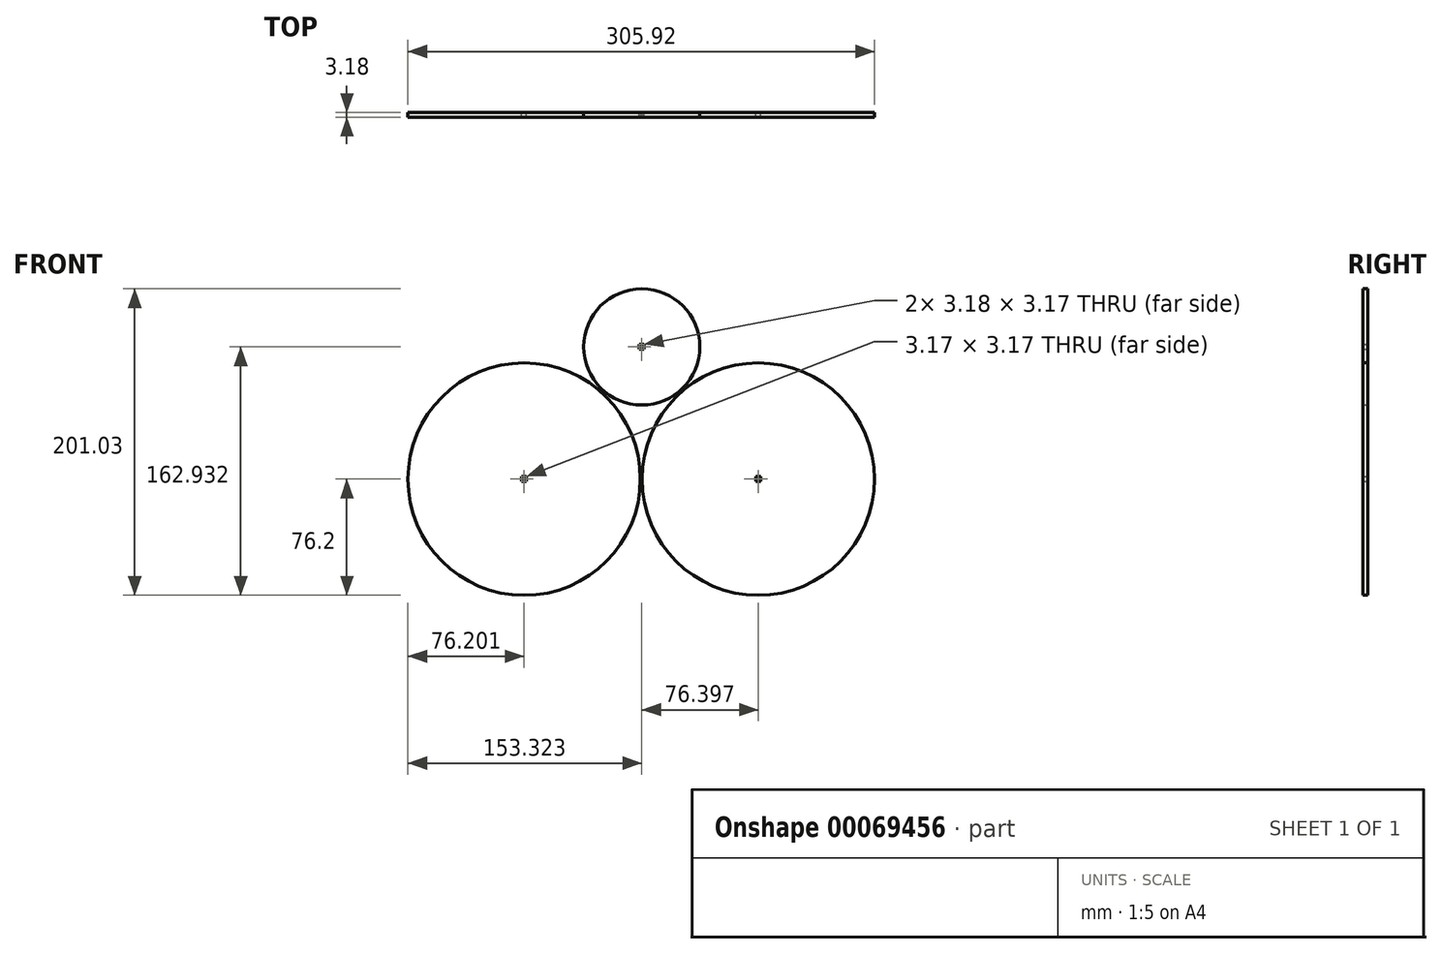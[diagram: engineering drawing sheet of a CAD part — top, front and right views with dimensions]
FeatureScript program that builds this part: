
annotation { "Feature Type Name" : "Feature", "Feature Type Description" : "" }
export const myFeature = defineFeature(function(context is Context, id is Id, definition is map)
    precondition{}
    {
        {
            var Q0;
            Q0=qCreatedBy(makeId("Front.planeOp"),FACE);
            var sketch = newSketch(context, id + "F0", { "sketchPlane" : qUnion([Q0])});
            skCircle(sketch, "E0", {"center": v(-95.2, 0) * mm, "radius": 76.2 * mm});
            skCircle(sketch, "E1", {"center": v(58.32, 0) * mm, "radius": 76.2 * mm});
            skCircle(sketch, "E2", {"center": v(-18.08, 86.73) * mm, "radius": 38.1 * mm});
            skLineSegment(sketch, "E3.bottom", {"start": v(56.73, 1.59) * mm, "end": v(59.9, 1.59) * mm});
            skLineSegment(sketch, "E3.top", {"start": v(56.73, -1.59) * mm, "end": v(59.9, -1.59) * mm});
            skLineSegment(sketch, "E3.left", {"start": v(56.73, 1.59) * mm, "end": v(56.73, -1.59) * mm});
            skLineSegment(sketch, "E3.right", {"start": v(59.9, 1.59) * mm, "end": v(59.9, -1.59) * mm});
            skLineSegment(sketch, "E4.bottom", {"start": v(-96.79, 1.59) * mm, "end": v(-93.61, 1.59) * mm});
            skLineSegment(sketch, "E4.top", {"start": v(-96.79, -1.59) * mm, "end": v(-93.61, -1.59) * mm});
            skLineSegment(sketch, "E4.left", {"start": v(-96.79, 1.59) * mm, "end": v(-96.79, -1.59) * mm});
            skLineSegment(sketch, "E4.right", {"start": v(-93.61, 1.59) * mm, "end": v(-93.61, -1.59) * mm});
            skLineSegment(sketch, "E5.bottom", {"start": v(-19.66, 88.32) * mm, "end": v(-16.49, 88.32) * mm});
            skLineSegment(sketch, "E5.top", {"start": v(-19.66, 85.14) * mm, "end": v(-16.49, 85.14) * mm});
            skLineSegment(sketch, "E5.left", {"start": v(-19.66, 88.32) * mm, "end": v(-19.66, 85.14) * mm});
            skLineSegment(sketch, "E5.right", {"start": v(-16.49, 88.32) * mm, "end": v(-16.49, 85.14) * mm});
            skSolve(sketch);
        }
        {
            var Q0;
            Q0=makeQuery(id+"F0.imprint","IMPRINT",FACE,{"disambiguationData":[TD([[makeQuery(id+"F0.imprint","IMPRINT",EDGE,{"derivedFrom":sQuery(id+"F0.wireOp",EDGE,"E0")}),1.0]])]});
            var Q1;
            Q1=makeQuery(id+"F0.imprint","IMPRINT",FACE,{"disambiguationData":[TD([[makeQuery(id+"F0.imprint","IMPRINT",EDGE,{"derivedFrom":sQuery(id+"F0.wireOp",EDGE,"E2")}),1.0]])]});
            var Q2;
            Q2=makeQuery(id+"F0.imprint","IMPRINT",FACE,{"disambiguationData":[TD([[makeQuery(id+"F0.imprint","IMPRINT",EDGE,{"derivedFrom":sQuery(id+"F0.wireOp",EDGE,"E1")}),1.0]])]});
            extrude(context, id + "F1", {"entities" : qUnion([Q0, Q1, Q2]), "depth" : 3.17 * mm});
        }
    });
